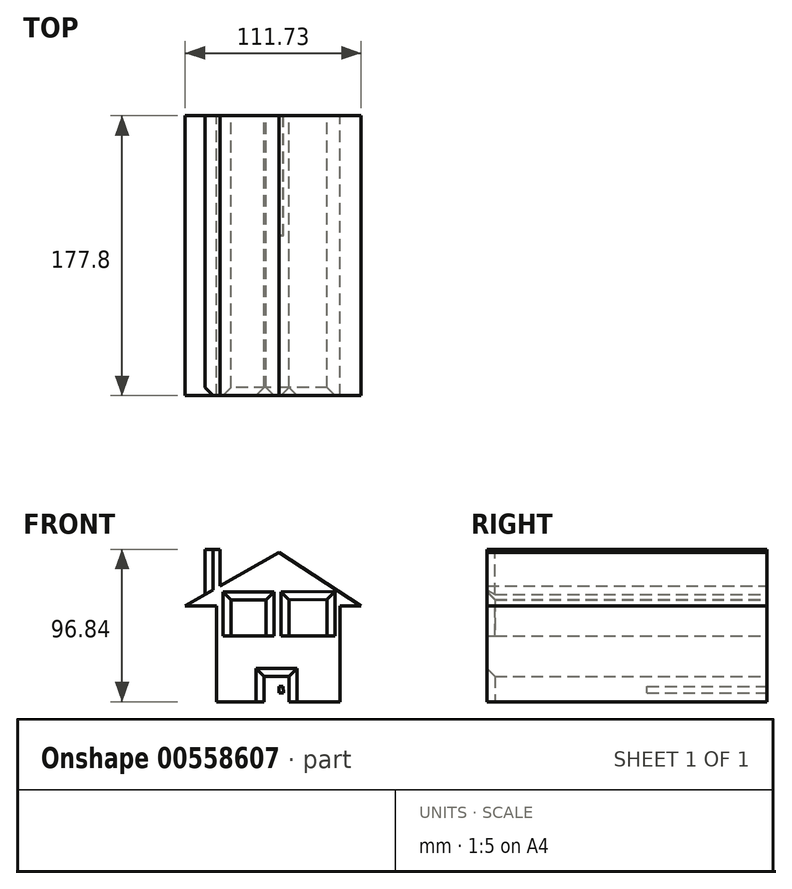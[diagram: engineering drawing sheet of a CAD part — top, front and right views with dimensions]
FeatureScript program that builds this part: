
annotation { "Feature Type Name" : "Feature", "Feature Type Description" : "" }
export const myFeature = defineFeature(function(context is Context, id is Id, definition is map)
    precondition{}
    {
        {
            var Q0;
            Q0=qCreatedBy(makeId("Front.planeOp"),FACE);
            var sketch = newSketch(context, id + "F0", { "sketchPlane" : qUnion([Q0])});
            skLineSegment(sketch, "E0", {"start": v(0, 48.93) * mm, "end": v(-59.6, 15.03) * mm});
            skLineSegment(sketch, "E1", {"start": v(-59.6, 15.03) * mm, "end": v(-39.56, 15.03) * mm});
            skLineSegment(sketch, "E2", {"start": v(-39.56, 15.03) * mm, "end": v(-39.56, -45.85) * mm});
            skLineSegment(sketch, "E3", {"start": v(-39.56, -45.85) * mm, "end": v(38.78, -45.85) * mm});
            skLineSegment(sketch, "E4", {"start": v(38.78, -45.85) * mm, "end": v(38.78, 15.03) * mm});
            skLineSegment(sketch, "E5", {"start": v(38.78, 15.03) * mm, "end": v(52.14, 15.03) * mm});
            skLineSegment(sketch, "E6", {"start": v(52.14, 15.03) * mm, "end": v(0, 48.93) * mm});
            skLineSegment(sketch, "E7", {"start": v(-9.5, -45.85) * mm, "end": v(-9.5, -29.67) * mm});
            skLineSegment(sketch, "E8", {"start": v(-9.5, -29.67) * mm, "end": v(6.42, -29.67) * mm});
            skLineSegment(sketch, "E9", {"start": v(6.42, -29.67) * mm, "end": v(6.42, -45.85) * mm});
            skLineSegment(sketch, "E10", {"start": v(6.42, 18.88) * mm, "end": v(6.42, -3.98) * mm});
            skPoint(sketch, "E10.startSnap0", {"position": v(6.42, -37.76) * mm});
            skLineSegment(sketch, "E11", {"start": v(6.42, -3.98) * mm, "end": v(30.57, -3.98) * mm});
            skLineSegment(sketch, "E12", {"start": v(30.57, -3.98) * mm, "end": v(30.57, 19.14) * mm});
            skLineSegment(sketch, "E13", {"start": v(30.57, 19.14) * mm, "end": v(6.42, 18.88) * mm});
            skLineSegment(sketch, "E14", {"start": v(-30.57, 22.22) * mm, "end": v(-30.57, -3.98) * mm});
            skLineSegment(sketch, "E15", {"start": v(-30.57, -3.98) * mm, "end": v(-8.22, -3.98) * mm});
            skLineSegment(sketch, "E16", {"start": v(-8.22, -3.98) * mm, "end": v(-8.22, 18.88) * mm});
            skLineSegment(sketch, "E17", {"start": v(-8.22, 18.88) * mm, "end": v(-30.57, 18.88) * mm});
            skLineSegment(sketch, "E18", {"start": v(-37.36, 27.68) * mm, "end": v(-37.36, 50.99) * mm});
            skLineSegment(sketch, "E19", {"start": v(-37.36, 50.99) * mm, "end": v(-47, 50.99) * mm});
            skLineSegment(sketch, "E20", {"start": v(-47, 50.99) * mm, "end": v(-47, 22.19) * mm});
            skLineSegment(sketch, "E21", {"start": v(-19.4, 18.88) * mm, "end": v(-19.4, -3.98) * mm});
            skLineSegment(sketch, "E22", {"start": v(-8.22, 7.45) * mm, "end": v(-30.57, 7.45) * mm});
            skLineSegment(sketch, "E23", {"start": v(17.98, 7.45) * mm, "end": v(17.98, 19) * mm});
            skPoint(sketch, "E23.startSnap0", {"position": v(6.42, 7.45) * mm});
            skLineSegment(sketch, "E24", {"start": v(17.98, 19) * mm, "end": v(17.98, -3.98) * mm});
            skLineSegment(sketch, "E25", {"start": v(17.98, -3.98) * mm, "end": v(17.98, 7.45) * mm});
            skLineSegment(sketch, "E26", {"start": v(30.57, 7.58) * mm, "end": v(6.42, 7.45) * mm});
            skLineSegment(sketch, "E27", {"start": v(2.57, -36.09) * mm, "end": v(0, -36.09) * mm});
            skLineSegment(sketch, "E28", {"start": v(0, -36.09) * mm, "end": v(0, -40.2) * mm});
            skLineSegment(sketch, "E29", {"start": v(0, -40.2) * mm, "end": v(2.83, -40.2) * mm});
            skLineSegment(sketch, "E30", {"start": v(2.83, -40.2) * mm, "end": v(2.57, -36.09) * mm});
            skSolve(sketch);
        }
        {
            var Q0;
            {var subQ0=sQuery(id+"F0.wireOp",EDGE,"E18");Q0=makeQuery(id+"F0.imprint","IMPRINT",FACE,{"disambiguationData":[TD([[makeQuery(id+"F0.imprint","IMPRINT",EDGE,{"derivedFrom":subQ0}),1.0]])]});}
            var Q1;
            Q1=makeQuery(id+"F0.imprint","IMPRINT",FACE,{"disambiguationData":[TD([[makeQuery(id+"F0.imprint","IMPRINT",EDGE,{"derivedFrom":sQuery(id+"F0.wireOp",EDGE,"E27")}),1.0]])]});
            var Q2;
            {var subQ20=sQuery(id+"F0.wireOp",EDGE,"E1");Q2=makeQuery(id+"F0.imprint","IMPRINT",FACE,{"disambiguationData":[TD([[makeQuery(id+"F0.imprint","IMPRINT",EDGE,{"derivedFrom":subQ20}),1.0]])]});}
            extrude(context, id + "F1", {"entities" : qUnion([Q0, Q1, Q2]), "depth" : 76.2 * mm, "offsetDistance" : 25.4 * mm});
        }
        {
            var Q0;
            Q0=makeQuery(id+"F1.opExtrude","CAP_FACE",FACE,{"disambiguationData":[OSD([sQuery(id+"F0.wireOp",EDGE,"E0"),sQuery(id+"F0.wireOp",EDGE,"E1"),sQuery(id+"F0.wireOp",EDGE,"E2"),sQuery(id+"F0.wireOp",EDGE,"E3"),sQuery(id+"F0.wireOp",EDGE,"E4"),sQuery(id+"F0.wireOp",EDGE,"E5"),sQuery(id+"F0.wireOp",EDGE,"E6"),sQuery(id+"F0.wireOp",EDGE,"E7"),sQuery(id+"F0.wireOp",EDGE,"E8"),sQuery(id+"F0.wireOp",EDGE,"E9"),sQuery(id+"F0.wireOp",EDGE,"E10"),sQuery(id+"F0.wireOp",EDGE,"E11"),sQuery(id+"F0.wireOp",EDGE,"E12"),sQuery(id+"F0.wireOp",EDGE,"E13"),sQuery(id+"F0.wireOp",EDGE,"E14"),sQuery(id+"F0.wireOp",EDGE,"E15"),sQuery(id+"F0.wireOp",EDGE,"E16"),sQuery(id+"F0.wireOp",EDGE,"E17"),sQuery(id+"F0.wireOp",EDGE,"E18"),sQuery(id+"F0.wireOp",EDGE,"E19"),sQuery(id+"F0.wireOp",EDGE,"E20")])],"isStart":false});
            var sketch = newSketch(context, id + "F2", { "sketchPlane" : qUnion([Q0])});
            skSolve(sketch);
        }
        {
            var Q0;
            Q0 = qSketchRegion(id + "F2", true);
            var Q1;
            {var subQ3=sQuery(id+"F0.wireOp",EDGE,"E1");Q1=makeQuery(id+"F2.imprint","IMPRINT",FACE,{"disambiguationData":[TD([[makeQuery(id+"F2.imprint","IMPRINT",EDGE,{"derivedFrom":makeQuery(id+"F1.opExtrude","CAP_EDGE",EDGE,{"disambiguationData":[OSD([subQ3])],"isStart":false})}),1.0]])]});}
            extrude(context, id + "F3", {"entities" : qUnion([Q0, Q1]), "operationType" : NewBodyOperationType.ADD, "depth" : 101.6 * mm, "offsetDistance" : 25.4 * mm});
        }
        {
            var Q0;
            Q0=makeQuery(id+"F3.opExtrude","CAP_EDGE",EDGE,{"disambiguationData":[OSD([sQuery(id+"F0.wireOp",EDGE,"E14")])],"isStart":false});
            var Q1;
            Q1=makeQuery(id+"F3.opExtrude","CAP_EDGE",EDGE,{"disambiguationData":[OSD([sQuery(id+"F0.wireOp",EDGE,"E17")])],"isStart":false});
            var Q2;
            Q2=makeQuery(id+"F3.opExtrude","CAP_EDGE",EDGE,{"disambiguationData":[OSD([sQuery(id+"F0.wireOp",EDGE,"E16")])],"isStart":false});
            var Q3;
            Q3=makeQuery(id+"F3.opExtrude","CAP_EDGE",EDGE,{"disambiguationData":[OSD([sQuery(id+"F0.wireOp",EDGE,"E10")])],"isStart":false});
            var Q4;
            Q4=makeQuery(id+"F3.opExtrude","CAP_EDGE",EDGE,{"disambiguationData":[OSD([sQuery(id+"F0.wireOp",EDGE,"E13")])],"isStart":false});
            var Q5;
            Q5=makeQuery(id+"F3.opExtrude","CAP_EDGE",EDGE,{"disambiguationData":[OSD([sQuery(id+"F0.wireOp",EDGE,"E12")])],"isStart":false});
            var Q6;
            Q6=makeQuery(id+"F3.opExtrude","CAP_EDGE",EDGE,{"disambiguationData":[OSD([sQuery(id+"F0.wireOp",EDGE,"E8")])],"isStart":false});
            var Q7;
            Q7=makeQuery(id+"F3.opExtrude","CAP_EDGE",EDGE,{"disambiguationData":[OSD([sQuery(id+"F0.wireOp",EDGE,"E7")])],"isStart":false});
            var Q8;
            Q8=makeQuery(id+"F3.opExtrude","CAP_EDGE",EDGE,{"disambiguationData":[OSD([sQuery(id+"F0.wireOp",EDGE,"E9")])],"isStart":false});
            chamfer(context, id + "F4", {"entities" : qUnion([Q0, Q1, Q2, Q3, Q4, Q5, Q6, Q7, Q8]), "width" : 5.08 * mm, "tangentPropagation" : true});
        }
        {
            var Q0;
            Q0=makeQuery(id+"F3.opExtrude","CAP_EDGE",EDGE,{"disambiguationData":[OSD([sQuery(id+"F0.wireOp",EDGE,"E20")])],"isStart":false});
            chamfer(context, id + "F5", {"entities" : qUnion([Q0]), "width" : 5.08 * mm, "tangentPropagation" : true});
        }
    });
